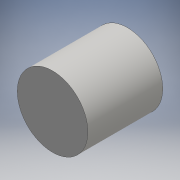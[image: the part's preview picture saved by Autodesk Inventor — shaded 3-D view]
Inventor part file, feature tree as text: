
AUTODESK INVENTOR PART (.ipt)
format: ipt  version: 2016 (Build 200138000, 138)  size: 86,016 bytes
history: native  units: mm
features: extrude x1, sketch x1
ambient origin geometry x8: Origin, YZ Plane, XZ Plane, XY Plane, X Axis, Y Axis, Z Axis, Center Point
bodies: Solid1 (feature_tree)
feature tree (2):
  extrude  "Extrusion1"  Depth=4.5mm TaperAngle=0.0deg
  sketch  "Sketch1"  dims[d0=4.25mm d1=4.5mm d2=0.0mm]
